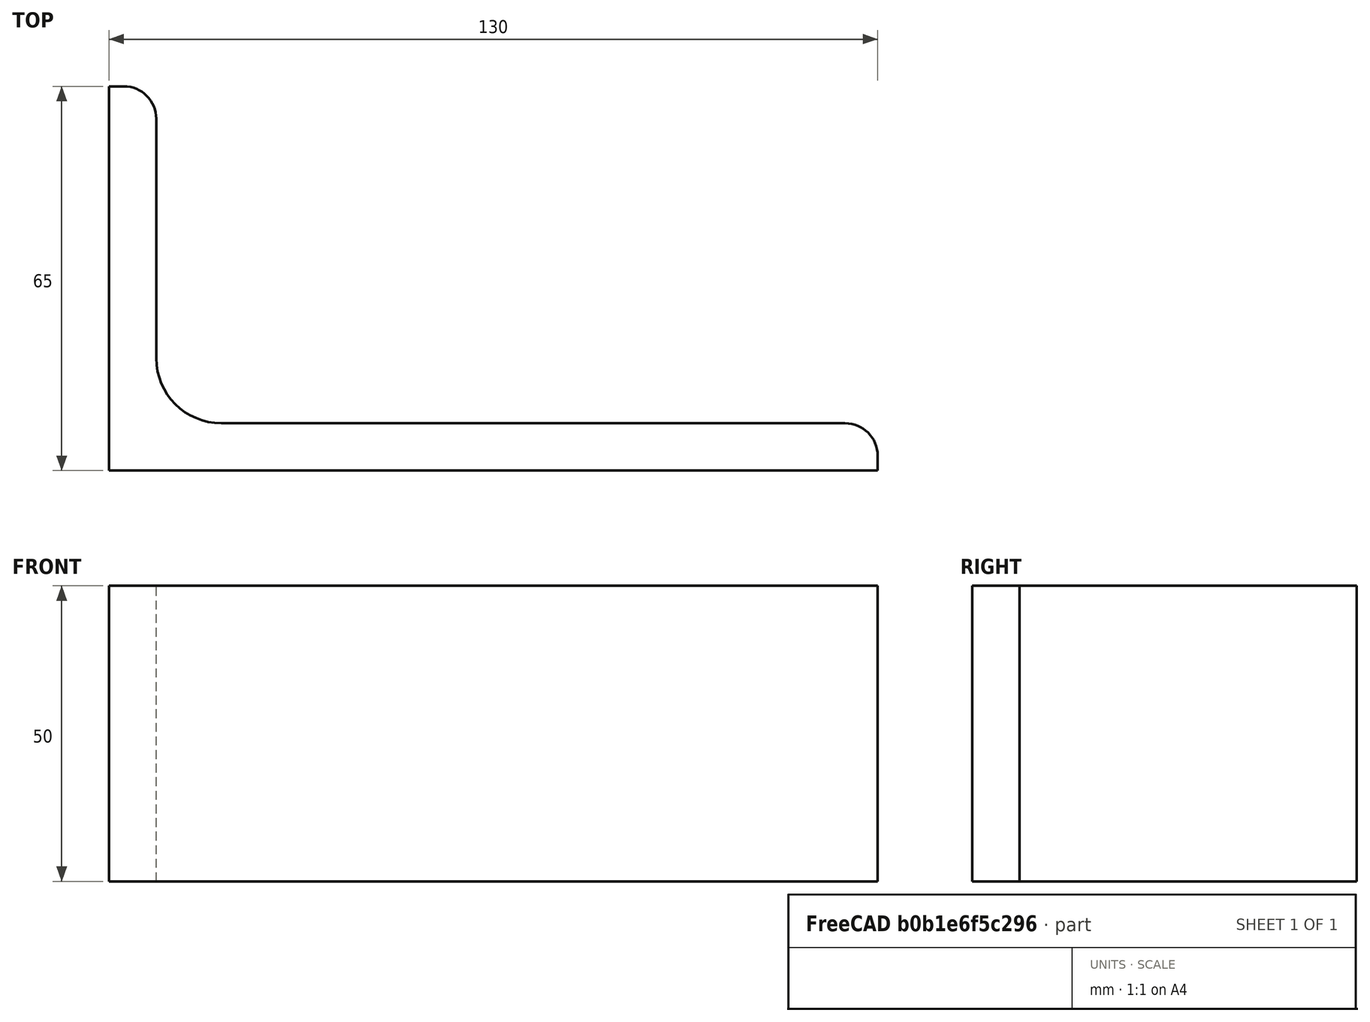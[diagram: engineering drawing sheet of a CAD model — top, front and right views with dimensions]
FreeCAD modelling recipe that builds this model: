
FCSTD DOCUMENT  (FreeCAD 0.15R4671 (Git))
Label: Angle Bar 130x65x8 EN10056 S235JR
License: All rights reserved
LicenseURL: http://en.wikipedia.org/wiki/All_rights_reserved
objects: Sketcher::SketchObject×1, Part::Extrusion×1
note: 2 computed .brp shape members not serialized (recipe doc carries the construction recipe); baked Part::Feature solids carry a one-line shape summary decoded from their .brp

FEATURE [Sketcher::SketchObject] Sketch
  sketch-geometry (9):
    g0: LineSegment StartX=0 StartY=0 StartZ=0 EndX=130 EndY=0 EndZ=0
    g1: LineSegment StartX=130 StartY=0 StartZ=0 EndX=130 EndY=2.5 EndZ=0
    g2: LineSegment StartX=124.5 StartY=8 StartZ=0 EndX=19 EndY=8 EndZ=0
    g3: LineSegment StartX=0 StartY=0 StartZ=0 EndX=0 EndY=65 EndZ=0
    g4: LineSegment StartX=0 StartY=65 StartZ=0 EndX=2.5 EndY=65 EndZ=0
    g5: LineSegment StartX=8 StartY=59.5 StartZ=0 EndX=8 EndY=19 EndZ=0
    g6: ArcOfCircle CenterX=19 CenterY=19 CenterZ=0 NormalX=0 NormalY=0 NormalZ=1 Radius=11 StartAngle=3.14159 EndAngle=4.71239
    g7: ArcOfCircle CenterX=2.5 CenterY=59.5 CenterZ=0 NormalX=0 NormalY=0 NormalZ=1 Radius=5.5 StartAngle=0 EndAngle=1.5708
    g8: ArcOfCircle CenterX=124.5 CenterY=2.5 CenterZ=0 NormalX=0 NormalY=0 NormalZ=1 Radius=5.5 StartAngle=0 EndAngle=1.5708
  constraints (23):
    c: Coincident(g0,g-1)
    c: Horizontal(g0)
    c: Coincident(g1,g0)
    c: Vertical(g1)
    c: Horizontal(g2)
    c: Coincident(g3,g-1)
    c: Vertical(g3)
    c: Coincident(g4,g3)
    c: Horizontal(g4)
    c: Vertical(g5)
    c: Tangent(g5,g6) = -1.5708
    c: Tangent(g2,g6) = 1.5708
    c: Tangent(g4,g7) = 1.5708
    c: Tangent(g5,g7) = 1.5708
    c: Tangent(g2,g8) = -1.5708
    c: Tangent(g1,g8) = -1.5708
    c: DistanceX(g0) = 130
    c: DistanceY(g3) = 65
    c: DistanceY(g0,g2) = 8
    c: DistanceX(g3,g5) = 8
    c: Radius(g6) = 11
    c: Radius(g8) = 5.5
    c: Radius(g7) = 5.5
FEATURE [Part::Extrusion] Extrude  label="Angle Bar 130x65x8 EN10056 S235JR"
  Base = -> Sketch
  Dir = (0,0,50)
  Solid = true
